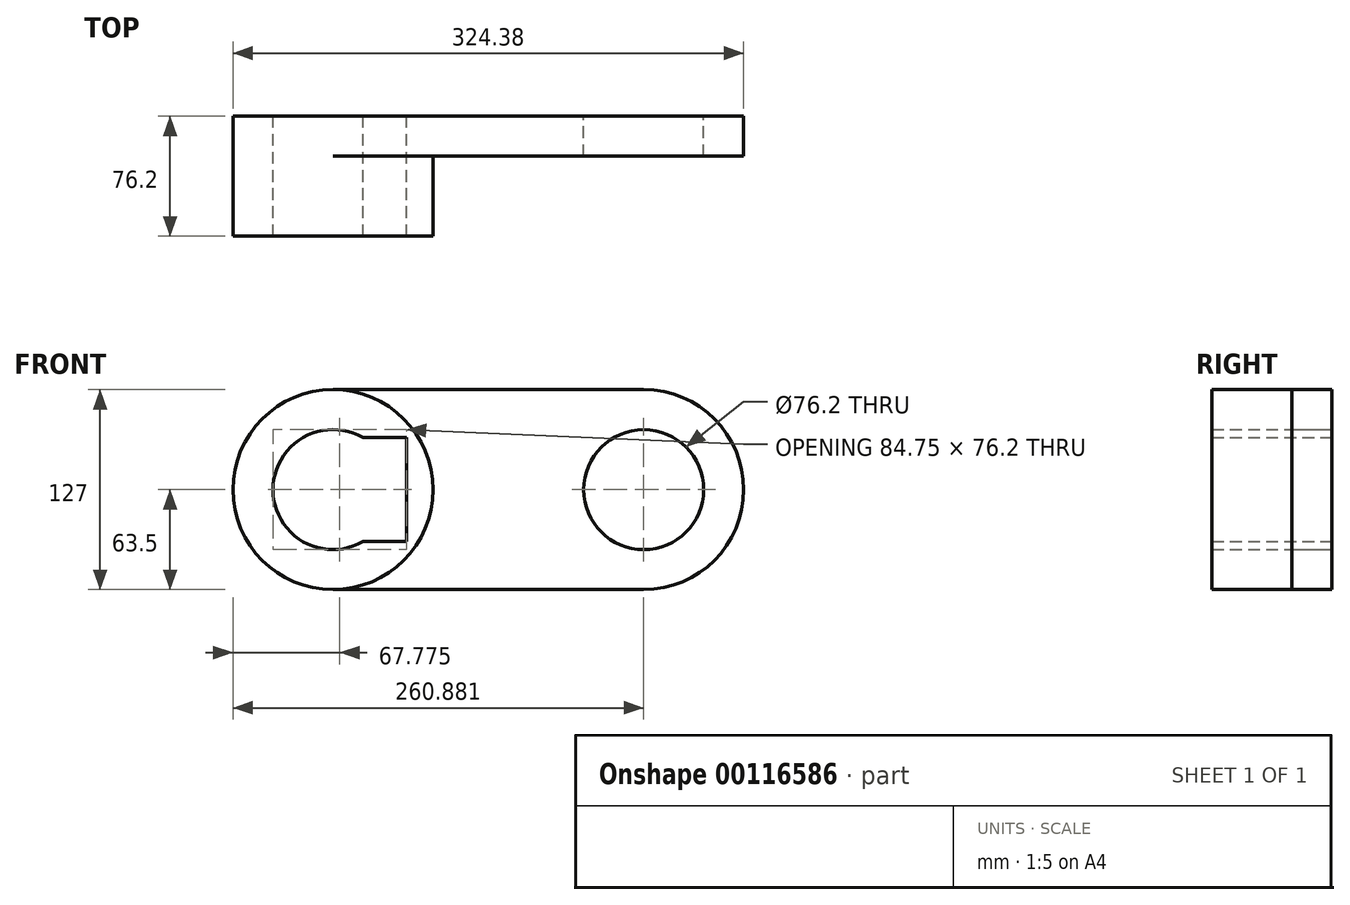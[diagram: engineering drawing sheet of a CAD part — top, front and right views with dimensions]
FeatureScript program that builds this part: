
annotation { "Feature Type Name" : "Feature", "Feature Type Description" : "" }
export const myFeature = defineFeature(function(context is Context, id is Id, definition is map)
    precondition{}
    {
        {
            var Q0;
            Q0=qCreatedBy(makeId("Front.planeOp"),FACE);
            var sketch = newSketch(context, id + "F0", { "sketchPlane" : qUnion([Q0])});
            skCircle(sketch, "E0", {"center": v(0, 0) * mm, "radius": 63.5 * mm});
            skCircle(sketch, "E1", {"center": v(197.38, 0) * mm, "radius": 63.5 * mm});
            skLineSegment(sketch, "E2", {"start": v(0, 63.5) * mm, "end": v(197.38, 63.5) * mm});
            skLineSegment(sketch, "E3", {"start": v(0, -63.5) * mm, "end": v(197.38, -63.5) * mm});
            skCircle(sketch, "E4", {"center": v(0, 0) * mm, "radius": 38.1 * mm});
            skCircle(sketch, "E5", {"center": v(197.38, 0) * mm, "radius": 38.1 * mm});
            skLineSegment(sketch, "E6.bottom", {"start": v(46.65, 33.01) * mm, "end": v(-46.65, 33.01) * mm});
            skLineSegment(sketch, "E6.top", {"start": v(46.65, -33.01) * mm, "end": v(-46.65, -33.01) * mm});
            skLineSegment(sketch, "E6.left", {"start": v(46.65, 33.01) * mm, "end": v(46.65, -33.01) * mm});
            skLineSegment(sketch, "E6.right", {"start": v(-46.65, 33.01) * mm, "end": v(-46.65, -33.01) * mm});
            skSolve(sketch);
        }
        {
            var Q0;
            {var subQ11=sQuery(id+"F0.wireOp",EDGE,"E6.left");Q0=makeQuery(id+"F0.imprint","IMPRINT",FACE,{"disambiguationData":[TD([[makeQuery(id+"F0.imprint","IMPRINT",EDGE,{"derivedFrom":subQ11}),1.0]])]});}
            var Q1;
            {var subQ5=sQuery(id+"F0.wireOp",EDGE,"E6.right");Q1=makeQuery(id+"F0.imprint","IMPRINT",FACE,{"disambiguationData":[TD([[makeQuery(id+"F0.imprint","IMPRINT",EDGE,{"derivedFrom":subQ5}),1.0]])]});}
            var Q2;
            {var subQ0=sQuery(id+"F0.wireOp",EDGE,"E2");Q2=makeQuery(id+"F0.imprint","IMPRINT",FACE,{"disambiguationData":[TD([[makeQuery(id+"F0.imprint","IMPRINT",EDGE,{"derivedFrom":subQ0}),-1.0]])]});}
            var Q3;
            Q3=makeQuery(id+"F0.imprint","IMPRINT",FACE,{"disambiguationData":[TD([[makeQuery(id+"F0.imprint","IMPRINT",EDGE,{"derivedFrom":sQuery(id+"F0.wireOp",EDGE,"E5")}),-1.0]])]});
            extrude(context, id + "F1", {"entities" : qUnion([Q0, Q1, Q2, Q3]), "depth" : 25.4 * mm});
        }
        {
            var Q0;
            {var subQ5=sQuery(id+"F0.wireOp",EDGE,"E6.right");Q0=makeQuery(id+"F0.imprint","IMPRINT",FACE,{"disambiguationData":[TD([[makeQuery(id+"F0.imprint","IMPRINT",EDGE,{"derivedFrom":subQ5}),1.0]])]});}
            var Q1;
            {var subQ11=sQuery(id+"F0.wireOp",EDGE,"E6.left");Q1=makeQuery(id+"F0.imprint","IMPRINT",FACE,{"disambiguationData":[TD([[makeQuery(id+"F0.imprint","IMPRINT",EDGE,{"derivedFrom":subQ11}),1.0]])]});}
            extrude(context, id + "F2", {"entities" : qUnion([Q0, Q1]), "operationType" : NewBodyOperationType.ADD, "depth" : 76.2 * mm});
        }
    });
